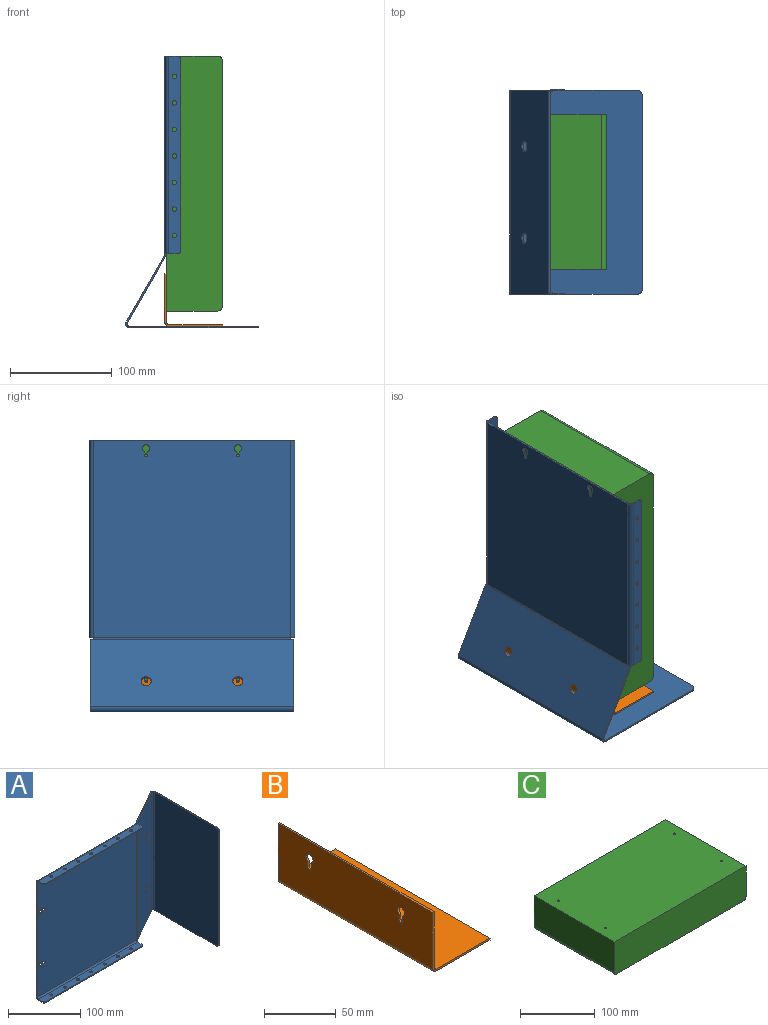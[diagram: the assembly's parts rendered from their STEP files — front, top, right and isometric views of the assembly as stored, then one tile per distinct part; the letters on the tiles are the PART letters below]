
ASSEMBLY  parts=3 mates=5
PART A: 70 faces, bbox 266.6x129.9x201.6 mm
  f0: plane 121.04x1.6mm, normal (0,0,-1), area 193.7mm2, adj f4,f5,f6,f66
  f1: plane 121.04x1.6mm, normal (0,0,1), area 193.7mm2, adj f2,f5,f6,f67
  f2: cylinder r=5mm len=5mm, axis (-1,0,0), area 12.6mm2, adj f1,f3,f5,f6
  f3: plane 190x1.6mm, normal (0,-1,0), area 304mm2, adj f2,f4,f5,f6
  f4: cylinder r=5mm len=5mm, axis (-1,0,0), area 12.6mm2, adj f0,f3,f5,f6
  f5: plane 200x126.04mm, normal (1,0,0), area 25196.6mm2, adj f0,f1,f2,f3,f4,f68
  f6: plane 200x126.04mm, normal (-1,0,0), area 25196.6mm2, adj f0,f1,f2,f3,f4,f69
  f7: plane 3.1x1.39mm, normal (-0.87,-0.5,0), area 5mm2, adj f8,f13,f14,f63
  f8: plane 66.45x38.91mm, normal (0,0,1), area 121mm2, adj f7,f13,f14,f67
  f9: plane 66.45x38.91mm, normal (0,0,-1), area 121mm2, adj f12,f13,f14,f66
  f10: cylinder r=5mm len=10mm, axis (0.5,-0.87,0), area 50.3mm2, adj f13,f14
  f11: cylinder r=5mm len=10mm, axis (0.5,-0.87,0), area 50.3mm2, adj f13,f14
  f12: plane 3.1x1.39mm, normal (-0.87,-0.5,0), area 5mm2, adj f9,f13,f14,f62
  f13: plane 200x65.66mm, normal (-0.5,0.87,0), area 14967.6mm2, adj f7,f8,f9,f10,f11,f12,f65,f68
  f14: plane 200x65.66mm, normal (0.5,-0.87,0), area 14967.6mm2, adj f7,f8,f9,f10,f11,f12,f64,f69
  f15: plane 193.8x1.6mm, normal (-1,0,0), area 310.1mm2, adj f24,f25,f40,f59
  f16: plane 3.89x1.6mm, normal (0,0,1), area 6.2mm2, adj f17,f23,f24,f25
  f17: cylinder r=1.6mm len=3.2mm, axis (0,-1,0), area 8mm2, adj f16,f18,f24,f25
  f18: plane 3.89x1.6mm, normal (0,0,-1), area 6.2mm2, adj f17,f23,f24,f25
  f19: plane 3.89x1.6mm, normal (0,0,-1), area 6.2mm2, adj f20,f22,f24,f25
  f20: cylinder r=3.5mm len=7mm, axis (0,-1,0), area 29.9mm2, adj f19,f21,f24,f25
  f21: plane 3.89x1.6mm, normal (0,0,1), area 6.2mm2, adj f20,f22,f24,f25
  f22: cylinder r=1.6mm len=3.2mm, axis (0,-1,0), area 8mm2, adj f19,f21,f24,f25
  f23: cylinder r=3.5mm len=7mm, axis (0,-1,0), area 29.9mm2, adj f16,f18,f24,f25
  f24: plane 193.96x193.8mm, normal (0,1,0), area 37482.1mm2, adj f15,f16,f17,f18,f19,f20,f21,f22
  f25: plane 193.96x193.8mm, normal (0,-1,0), area 37482.1mm2, adj f15,f16,f17,f18,f19,f20,f21,f22
  f26: plane 189.96x1.6mm, normal (0,-1,0), area 303.9mm2, adj f27,f37,f38,f39
  f27: cylinder r=2mm len=2mm, axis (0,0,-1), area 5mm2, adj f26,f28,f38,f39
  f28: plane 9.1x1.6mm, normal (-1,0,0), area 14.6mm2, adj f27,f38,f39,f40
  f29: plane 9.1x1.6mm, normal (1,0,0), area 14.6mm2, adj f37,f38,f39,f41
  f30: cylinder r=2.1mm len=4.2mm, axis (0,0,-1), area 21.1mm2, adj f38,f39
  f31: cylinder r=2.1mm len=4.2mm, axis (0,0,-1), area 21.1mm2, adj f38,f39
  f32: cylinder r=2.1mm len=4.2mm, axis (0,0,-1), area 21.1mm2, adj f38,f39
  f33: cylinder r=2.1mm len=4.2mm, axis (0,0,-1), area 21.1mm2, adj f38,f39
  f34: cylinder r=2.1mm len=4.2mm, axis (0,0,-1), area 21.1mm2, adj f38,f39
  f35: cylinder r=2.1mm len=4.2mm, axis (0,0,-1), area 21.1mm2, adj f38,f39
  f36: cylinder r=2.1mm len=4.2mm, axis (0,0,-1), area 21.1mm2, adj f38,f39
  f37: cylinder r=2mm len=2mm, axis (0,0,-1), area 5mm2, adj f26,f29,f38,f39
  f38: plane 193.96x11.1mm, normal (0,0,-1), area 2054.3mm2, adj f26,f27,f28,f29,f30,f31,f32,f33
  f39: plane 193.96x11.1mm, normal (0,0,1), area 2054.3mm2, adj f26,f27,f28,f29,f30,f31,f32,f33
  f40: plane 3.9x3.9mm, normal (-1,0,0), area 7.8mm2, adj f15,f28,f42,f43
  f41: plane 3.9x3.9mm, normal (1,0,0), area 7.8mm2, adj f29,f42,f43,f62
  f42: cylinder r=3.9mm len=193.96mm, axis (-1,0,0), area 1188.2mm2, adj f24,f38,f40,f41
  f43: cylinder r=2.3mm len=193.96mm, axis (-1,0,0), area 700.8mm2, adj f25,f39,f40,f41
  f44: plane 9.1x1.6mm, normal (1,0,0), area 14.6mm2, adj f55,f56,f57,f58
  f45: plane 9.1x1.6mm, normal (-1,0,0), area 14.6mm2, adj f46,f56,f57,f59
  f46: cylinder r=2mm len=2mm, axis (0,0,1), area 5mm2, adj f45,f47,f56,f57
  f47: plane 189.96x1.6mm, normal (0,-1,0), area 303.9mm2, adj f46,f55,f56,f57
  f48: cylinder r=2.1mm len=4.2mm, axis (0,0,1), area 21.1mm2, adj f56,f57
  f49: cylinder r=2.1mm len=4.2mm, axis (0,0,1), area 21.1mm2, adj f56,f57
  f50: cylinder r=2.1mm len=4.2mm, axis (0,0,1), area 21.1mm2, adj f56,f57
  f51: cylinder r=2.1mm len=4.2mm, axis (0,0,1), area 21.1mm2, adj f56,f57
  f52: cylinder r=2.1mm len=4.2mm, axis (0,0,1), area 21.1mm2, adj f56,f57
  f53: cylinder r=2.1mm len=4.2mm, axis (0,0,1), area 21.1mm2, adj f56,f57
  f54: cylinder r=2.1mm len=4.2mm, axis (0,0,1), area 21.1mm2, adj f56,f57
  f55: cylinder r=2mm len=2mm, axis (0,0,1), area 5mm2, adj f44,f47,f56,f57
  f56: plane 193.96x11.1mm, normal (0,0,1), area 2054.3mm2, adj f44,f45,f46,f47,f48,f49,f50,f51
  f57: plane 193.96x11.1mm, normal (0,0,-1), area 2054.3mm2, adj f44,f45,f46,f47,f48,f49,f50,f51
  f58: plane 3.9x3.9mm, normal (1,0,0), area 7.8mm2, adj f44,f60,f61,f63
  f59: plane 3.9x3.9mm, normal (-1,0,0), area 7.8mm2, adj f15,f45,f60,f61
  f60: cylinder r=3.9mm len=193.96mm, axis (1,0,0), area 1188.2mm2, adj f24,f56,f58,f59
  f61: cylinder r=2.3mm len=193.96mm, axis (1,0,0), area 700.8mm2, adj f25,f57,f58,f59
  f62: plane 1.94x1.9mm, normal (0,0,-1), area 2.6mm2, adj f12,f41,f64,f65
  f63: plane 1.94x1.9mm, normal (0,0,1), area 2.6mm2, adj f7,f58,f64,f65
  f64: cylinder r=3.9mm len=193.8mm, axis (0,0,-1), area 392.4mm2, adj f14,f25,f62,f63
  f65: cylinder r=2.3mm len=193.8mm, axis (0,0,-1), area 231.4mm2, adj f13,f24,f62,f63
  f66: plane 5.84x3.9mm, normal (0,0,-1), area 10.4mm2, adj f0,f9,f68,f69
  f67: plane 5.84x3.9mm, normal (0,0,1), area 10.4mm2, adj f1,f8,f68,f69
  f68: cylinder r=3.9mm len=200mm, axis (0,0,-1), area 1630.2mm2, adj f5,f13,f66,f67
  f69: cylinder r=2.3mm len=200mm, axis (0,0,-1), area 961.4mm2, adj f6,f14,f66,f67
PART B: 22 faces, bbox 56.6x152x51.6 mm
  f0: plane 4.89x1.6mm, normal (0,1,0), area 7.8mm2, adj f1,f10,f11,f12
  f1: cylinder r=1.6mm len=3.2mm, axis (-1,0,0), area 8mm2, adj f0,f2,f11,f12
  f2: plane 4.89x1.6mm, normal (0,-1,0), area 7.8mm2, adj f1,f10,f11,f12
  f3: plane 4.89x1.6mm, normal (0,1,0), area 7.8mm2, adj f4,f9,f11,f12
  f4: cylinder r=1.6mm len=3.2mm, axis (-1,0,0), area 8mm2, adj f3,f5,f11,f12
  f5: plane 4.89x1.6mm, normal (0,-1,0), area 7.8mm2, adj f4,f9,f11,f12
  f6: plane 47.7x1.6mm, normal (0,1,0), area 76.3mm2, adj f8,f11,f12,f19
  f7: plane 47.7x1.6mm, normal (0,-1,0), area 76.3mm2, adj f8,f11,f12,f18
  f8: plane 152x1.6mm, normal (0,0,1), area 243.2mm2, adj f6,f7,f11,f12
  f9: cylinder r=3.5mm len=7mm, axis (-1,0,0), area 29.9mm2, adj f3,f5,f11,f12
  f10: cylinder r=3.5mm len=7mm, axis (-1,0,0), area 29.9mm2, adj f0,f2,f11,f12
  f11: plane 152x47.7mm, normal (-1,0,0), area 7135.8mm2, adj f0,f1,f2,f3,f4,f5,f6,f7
  f12: plane 152x47.7mm, normal (1,0,0), area 7135.8mm2, adj f0,f1,f2,f3,f4,f5,f6,f7
  f13: plane 52.7x1.6mm, normal (0,1,0), area 84.3mm2, adj f14,f16,f17,f19
  f14: plane 152x1.6mm, normal (1,0,0), area 243.2mm2, adj f13,f15,f16,f17
  f15: plane 52.7x1.6mm, normal (0,-1,0), area 84.3mm2, adj f14,f16,f17,f18
  f16: plane 152x52.7mm, normal (0,0,-1), area 8010.4mm2, adj f13,f14,f15,f20
  f17: plane 152x52.7mm, normal (0,0,1), area 8010.4mm2, adj f13,f14,f15,f21
  f18: plane 3.9x3.9mm, normal (0,-1,0), area 7.8mm2, adj f7,f15,f20,f21
  f19: plane 3.9x3.9mm, normal (0,1,0), area 7.8mm2, adj f6,f13,f20,f21
  f20: cylinder r=3.9mm len=152mm, axis (0,-1,0), area 931.2mm2, adj f11,f16,f18,f19
  f21: cylinder r=2.3mm len=152mm, axis (0,-1,0), area 549.2mm2, adj f12,f17,f18,f19
PART C: 16 faces, bbox 250x152x55 mm
  f0: plane 250x152mm, normal (0,0,1), area 37971.7mm2, adj f1,f2,f3,f4,f6,f8,f10,f12
  f1: plane 250x55mm, normal (0,-1,0), area 13739.3mm2, adj f0,f2,f4,f5,f14,f15
  f2: plane 152x50mm, normal (1,0,0), area 7600mm2, adj f0,f1,f3,f14
  f3: plane 250x55mm, normal (0,1,0), area 13739.3mm2, adj f0,f2,f4,f5,f14,f15
  f4: plane 152x50mm, normal (-1,0,0), area 7600mm2, adj f0,f1,f3,f15
  f5: plane 240x152mm, normal (0,0,-1), area 36480mm2, adj f1,f3,f14,f15
  f6: cylinder r=1.5mm len=5mm, axis (0,0,1), area 47.1mm2, adj f0,f7
  f7: plane 3x3mm, normal (0,0,1), area 7.1mm2, adj f6
  f8: cylinder r=1.5mm len=5mm, axis (0,0,1), area 47.1mm2, adj f0,f9
  f9: plane 3x3mm, normal (0,0,1), area 7.1mm2, adj f8
  f10: cylinder r=1.5mm len=5mm, axis (0,0,1), area 47.1mm2, adj f0,f11
  f11: plane 3x3mm, normal (0,0,1), area 7.1mm2, adj f10
  f12: cylinder r=1.5mm len=5mm, axis (0,0,1), area 47.1mm2, adj f0,f13
  f13: plane 3x3mm, normal (0,0,1), area 7.1mm2, adj f12
  f14: cylinder r=5mm len=152mm, axis (0,1,0), area 1193.8mm2, adj f1,f2,f3,f5
  f15: cylinder r=5mm len=152mm, axis (0,-1,0), area 1193.8mm2, adj f1,f3,f4,f5
PLACE A rot(axis=(-0.58,0.58,0.58),120deg) t=(-83.3,289.45,353.78)mm
PLACE B rot(axis=(-0.09,-0.99,0.13),0deg) t=(-153.09,465.45,132.45)mm
PLACE C rot(axis=(0.71,0,-0.71),180deg) t=(-118.3,389.45,270.85)mm
MATE planar C.f0 <-> A.f25  axis (-1,0,0) through (-173.3,389.45,270.85)mm
MATE planar A.f6 <-> B.f16  axis (0,0,1) through (-146.34,389.45,130.85)mm
MATE planar B.f12 <-> C.f8  axis (1,0,0) through (-173.3,389.45,158.49)mm
MATE fastened C.f10 <-> A.f17  axis (-1,0,0) through (-173.3,434.45,380.85)mm
MATE planar C.f1 <-> B.f6  axis (0,1,0) through (-145.82,465.45,270.85)mm
